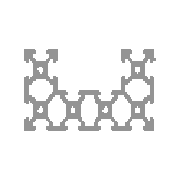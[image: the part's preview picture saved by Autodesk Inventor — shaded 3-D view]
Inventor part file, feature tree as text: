
AUTODESK INVENTOR PART (.ipt)
format: ipt  version: 2023.2 (Build 272271000, 271)  size: 1,272,832 bytes
history: native  units: mm
features: other x4, sketch x4, plane x1
ambient origin geometry x8: Origin, YZ Plane, XZ Plane, XY Plane, X Axis, Y Axis, Z Axis, Center Point
bodies: Body (feature_tree), Solid1 (feature_tree), Body1 (feature_tree)
feature tree (9):
  other  "Driven Length"
  other  "C-Beam-Extrusion.step"
  sketch  "Sketch plane"  dims[d5=0.13mm d6=0.0mm d7=90.0deg d8=0.1mm]
  other  "Start Plane"
  other  "End Plane"
  sketch  "Sketch1"  dims[d2=0.0mm]
  sketch  "Sketch2"  dims[d3=-0.0mm]
  plane  "Work Plane4"
  sketch  "Sketch3"  dims[d4=0.1mm]
